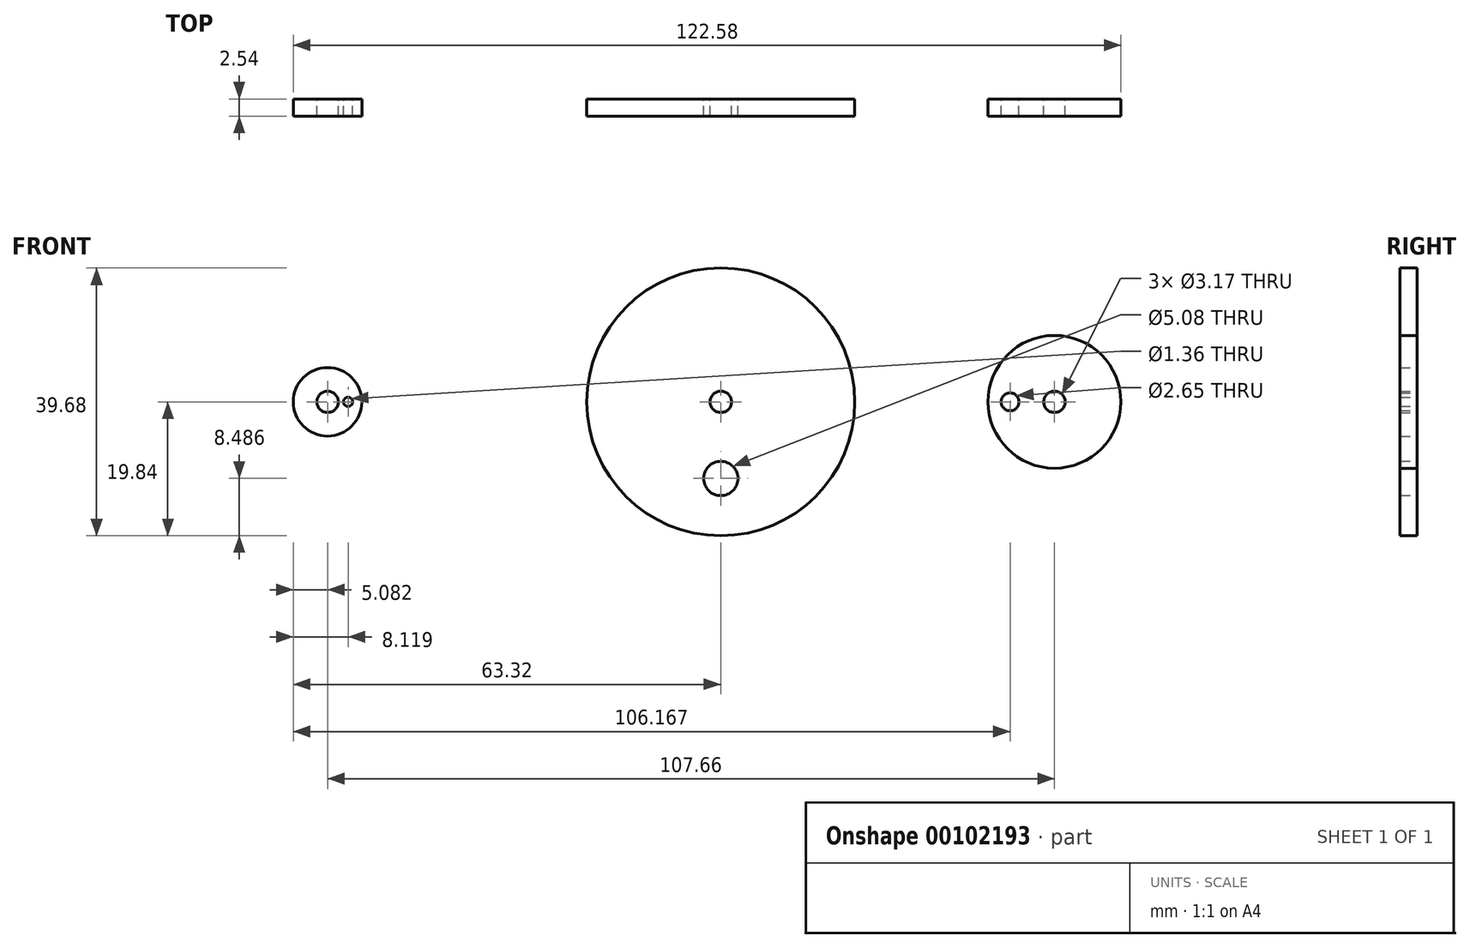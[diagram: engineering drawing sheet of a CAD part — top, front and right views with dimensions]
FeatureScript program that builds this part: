
annotation { "Feature Type Name" : "Feature", "Feature Type Description" : "" }
export const myFeature = defineFeature(function(context is Context, id is Id, definition is map)
    precondition{}
    {
        {
            var Q0;
            Q0=qCreatedBy(makeId("Front.planeOp"),FACE);
            var sketch = newSketch(context, id + "F0", { "sketchPlane" : qUnion([Q0])});
            skCircle(sketch, "E0", {"center": v(0, 0) * mm, "radius": 19.84 * mm});
            skCircle(sketch, "E1", {"center": v(-58.24, 0) * mm, "radius": 5.08 * mm});
            skCircle(sketch, "E2", {"center": v(49.42, 0) * mm, "radius": 9.84 * mm});
            skCircle(sketch, "E3", {"center": v(0, 0) * mm, "radius": 1.59 * mm});
            skCircle(sketch, "E4", {"center": v(-58.24, 0) * mm, "radius": 1.59 * mm});
            skCircle(sketch, "E5", {"center": v(49.42, 0) * mm, "radius": 1.59 * mm});
            skCircle(sketch, "E6", {"center": v(0, -11.35) * mm, "radius": 2.54 * mm});
            skCircle(sketch, "E7", {"center": v(-55.2, 0) * mm, "radius": 0.68 * mm});
            skCircle(sketch, "E8", {"center": v(42.85, 0) * mm, "radius": 1.32 * mm});
            skSolve(sketch);
        }
        {
            var Q0;
            Q0=makeQuery(id+"F0.imprint","IMPRINT",FACE,{"disambiguationData":[TD([[makeQuery(id+"F0.imprint","IMPRINT",EDGE,{"derivedFrom":sQuery(id+"F0.wireOp",EDGE,"E1")}),1.0]])]});
            var Q1;
            Q1=makeQuery(id+"F0.imprint","IMPRINT",FACE,{"disambiguationData":[TD([[makeQuery(id+"F0.imprint","IMPRINT",EDGE,{"derivedFrom":sQuery(id+"F0.wireOp",EDGE,"E2")}),1.0]])]});
            var Q2;
            Q2=makeQuery(id+"F0.imprint","IMPRINT",FACE,{"disambiguationData":[TD([[makeQuery(id+"F0.imprint","IMPRINT",EDGE,{"derivedFrom":sQuery(id+"F0.wireOp",EDGE,"E0")}),1.0]])]});
            extrude(context, id + "F1", {"entities" : qUnion([Q0, Q1, Q2]), "depth" : 2.54 * mm});
        }
    });
